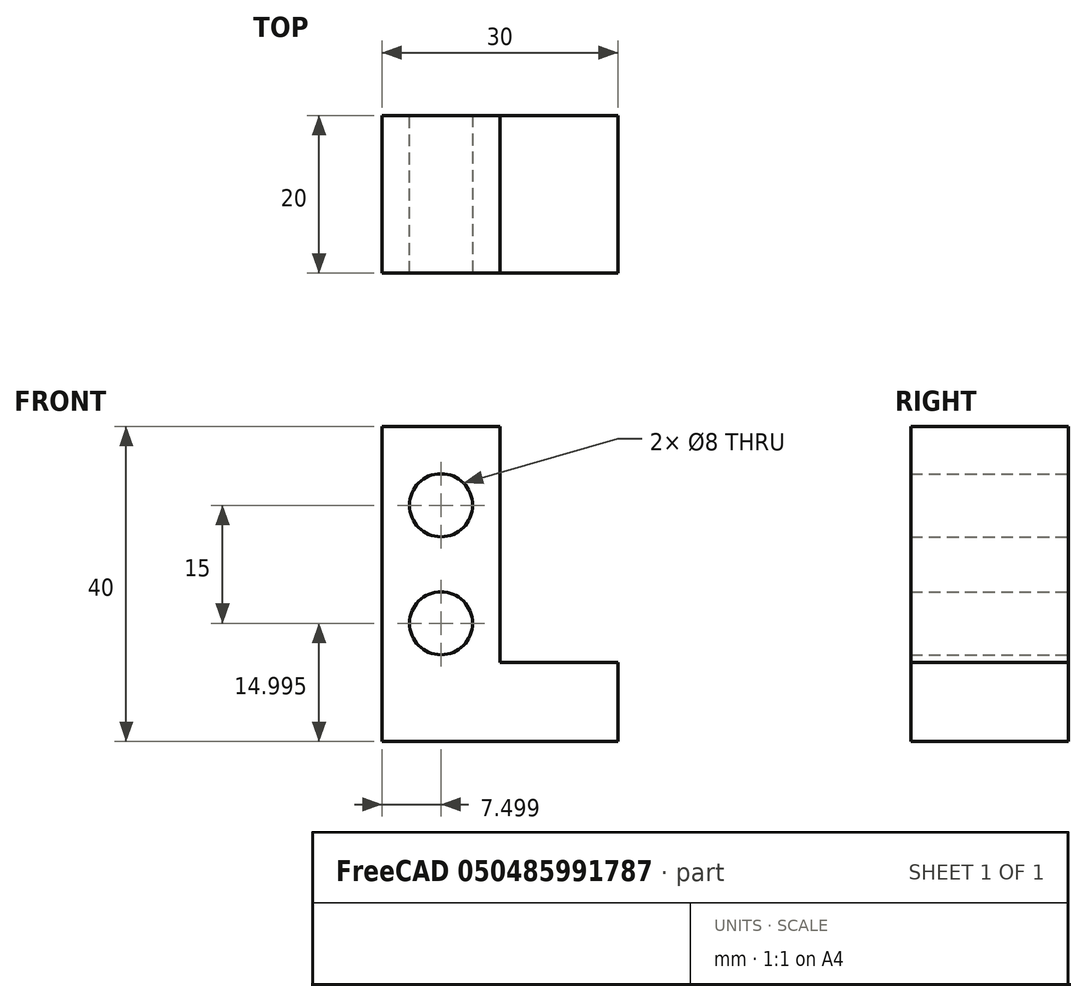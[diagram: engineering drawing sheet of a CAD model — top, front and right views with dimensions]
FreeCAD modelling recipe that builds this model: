
FCSTD DOCUMENT  (FreeCAD 0.15R4671 (Git))
Label: camion_superior_soporteEjeY
License: All rights reserved
LicenseURL: http://en.wikipedia.org/wiki/All_rights_reserved
objects: Sketcher::SketchObject×1, PartDesign::Pad×1
note: 3 computed .brp shape members not serialized (recipe doc carries the construction recipe); baked Part::Feature solids carry a one-line shape summary decoded from their .brp

FEATURE [Sketcher::SketchObject] Sketch
  Placement = pos=(0,0,0) rot=(0,0.707107,0.707107;4.71239rad)
  sketch-geometry (8):
    g0: LineSegment StartX=4.80865 StartY=9.30548 StartZ=0 EndX=-25.1914 EndY=9.30548 EndZ=0
    g1: LineSegment StartX=-25.1914 StartY=9.30548 StartZ=0 EndX=-25.1914 EndY=49.3055 EndZ=0
    g2: LineSegment StartX=-25.1914 StartY=49.3055 StartZ=0 EndX=-10.1914 EndY=49.3055 EndZ=0
    g3: LineSegment StartX=-10.1914 StartY=49.3055 StartZ=0 EndX=-10.1914 EndY=19.3055 EndZ=0
    g4: LineSegment StartX=-10.1914 StartY=19.3055 StartZ=0 EndX=4.80865 EndY=19.3055 EndZ=0
    g5: LineSegment StartX=4.80865 StartY=19.3055 StartZ=0 EndX=4.80865 EndY=9.30548 EndZ=0
    g6: Circle CenterX=-17.6914 CenterY=39.3055 CenterZ=0 NormalX=0 NormalY=0 NormalZ=1 Radius=4
    g7: Circle CenterX=-17.6914 CenterY=24.3055 CenterZ=0 NormalX=0 NormalY=0 NormalZ=1 Radius=4
  constraints (22):
    c: Horizontal(g0)
    c: Coincident(g0,g1)
    c: Vertical(g1)
    c: Coincident(g1,g2)
    c: Horizontal(g2)
    c: Coincident(g2,g3)
    c: Vertical(g3)
    c: Coincident(g3,g4)
    c: Horizontal(g4)
    c: Coincident(g4,g5)
    c: Coincident(g5,g0)
    c: DistanceX(g0) = -30
    c: DistanceX(g2) = 15
    c: DistanceX(g4) = 15
    c: DistanceY(g1) = 40
    c: DistanceY(g3) = -30
    c: Radius(g6) = 4
    c: Radius(g7) = 4
    c: DistanceX(g6,g2) = 7.5
    c: DistanceX(g7,g2) = 7.5
    c: DistanceY(g6,g7) = -15
    c: DistanceY(g6,g1) = 10
FEATURE [PartDesign::Pad] Pad
  Length = 20
  Length2 = 100
  Placement = pos=(0,0,0) rot=(1,0,0;1.5708rad)
  Sketch = -> Sketch
  Type = 0
